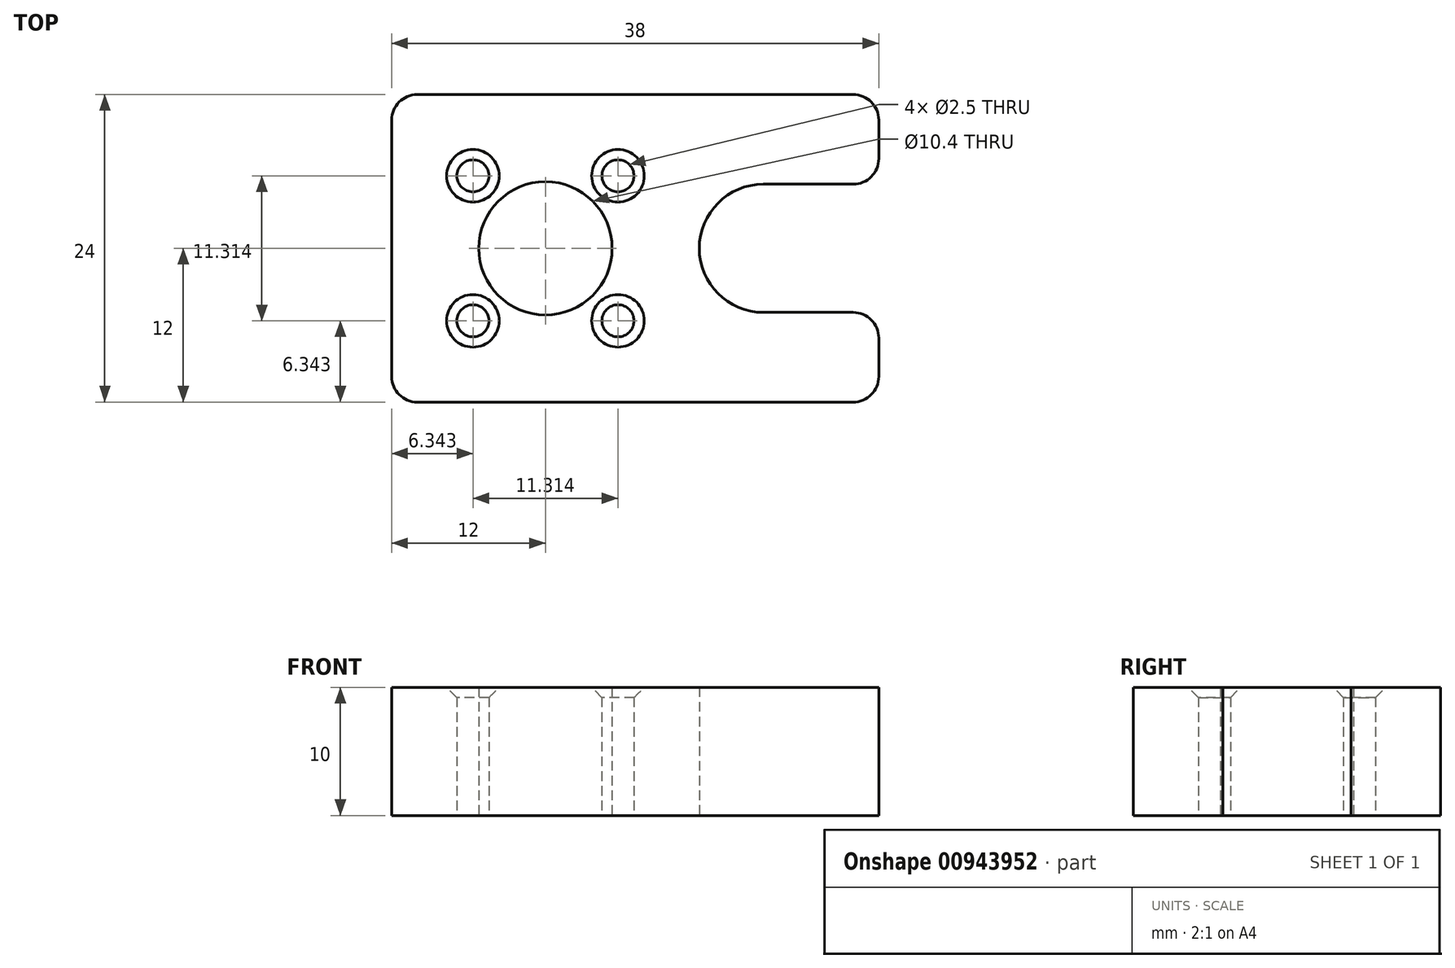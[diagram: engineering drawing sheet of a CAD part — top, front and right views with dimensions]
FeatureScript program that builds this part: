
annotation { "Feature Type Name" : "Feature", "Feature Type Description" : "" }
export const myFeature = defineFeature(function(context is Context, id is Id, definition is map)
    precondition{}
    {
        {
            var Q0;
            Q0=qCreatedBy(makeId("Top.planeOp"),FACE);
            var sketch = newSketch(context, id + "F0", { "sketchPlane" : qUnion([Q0])});
            skLineSegment(sketch, "E0.bottom", {"start": v(19, 12) * mm, "end": v(-19, 12) * mm});
            skLineSegment(sketch, "E0.top", {"start": v(19, -12) * mm, "end": v(-19, -12) * mm});
            skLineSegment(sketch, "E0.left", {"start": v(19, 12) * mm, "end": v(19, 5) * mm});
            skLineSegment(sketch, "E0.right", {"start": v(-19, 12) * mm, "end": v(-19, -12) * mm});
            skPoint(sketch, "E0.middle", {"position": v(0, 0) * mm});
            skCircle(sketch, "E1", {"center": v(-7, 0) * mm, "radius": 5.2 * mm});
            skCircle(sketch, "E2", {"center": v(10, 0) * mm, "radius": 5 * mm, "construction": true});
            skLineSegment(sketch, "E3", {"start": v(10, 5) * mm, "end": v(19, 5) * mm});
            skLineSegment(sketch, "E4", {"start": v(10, -5) * mm, "end": v(19, -5) * mm});
            skArc(sketch, "E5", {"start": v(10, 5) * mm, "mid": v(5, 0) * mm, "end": v(10, -5) * mm});
            skLineSegment(sketch, "E6.trimOffspring", {"start": v(19, -5) * mm, "end": v(19, -12) * mm});
            skCircle(sketch, "E7", {"center": v(-7, 0) * mm, "radius": 8 * mm, "construction": true});
            skLineSegment(sketch, "E8.bottom", {"start": v(-12.66, 5.66) * mm, "end": v(-1.34, 5.66) * mm, "construction": true});
            skLineSegment(sketch, "E8.top", {"start": v(-12.66, -5.66) * mm, "end": v(-1.34, -5.66) * mm, "construction": true});
            skLineSegment(sketch, "E8.left", {"start": v(-12.66, 5.66) * mm, "end": v(-12.66, -5.66) * mm, "construction": true});
            skLineSegment(sketch, "E8.right", {"start": v(-1.34, 5.66) * mm, "end": v(-1.34, -5.66) * mm, "construction": true});
            skCircle(sketch, "E9", {"center": v(-12.66, 5.66) * mm, "radius": 1.25 * mm});
            skCircle(sketch, "E10", {"center": v(-1.34, 5.66) * mm, "radius": 1.25 * mm});
            skCircle(sketch, "E11", {"center": v(-12.66, -5.66) * mm, "radius": 1.25 * mm});
            skCircle(sketch, "E12", {"center": v(-1.34, -5.66) * mm, "radius": 1.25 * mm});
            skCircle(sketch, "E13", {"center": v(-7, 0) * mm, "radius": 11 * mm, "construction": true});
            skSolve(sketch);
        }
        {
            var Q0;
            Q0 = qSketchRegion(id + "F0", true);
            extrude(context, id + "F1", {"entities" : qUnion([Q0]), "depth" : 10 * mm, "offsetDistance" : 25 * mm});
        }
        {
            var Q0;
            Q0=makeQuery(id+"F1.opExtrude","SWEPT_EDGE",EDGE,{"disambiguationData":[OSD([sQuery(id+"F0.wireOp",EDGE,"E0.top"),sQuery(id+"F0.wireOp",EDGE,"E0.right")])]});
            var Q1;
            Q1=makeQuery(id+"F1.opExtrude","SWEPT_EDGE",EDGE,{"disambiguationData":[OSD([sQuery(id+"F0.wireOp",EDGE,"E0.bottom"),sQuery(id+"F0.wireOp",EDGE,"E0.right")])]});
            var Q2;
            Q2=makeQuery(id+"F1.opExtrude","SWEPT_EDGE",EDGE,{"disambiguationData":[OSD([sQuery(id+"F0.wireOp",EDGE,"E0.top"),sQuery(id+"F0.wireOp",EDGE,"E6.trimOffspring")])]});
            var Q3;
            Q3=makeQuery(id+"F1.opExtrude","SWEPT_EDGE",EDGE,{"disambiguationData":[OSD([sQuery(id+"F0.wireOp",EDGE,"E4"),sQuery(id+"F0.wireOp",EDGE,"E6.trimOffspring")])]});
            var Q4;
            Q4=makeQuery(id+"F1.opExtrude","SWEPT_EDGE",EDGE,{"disambiguationData":[OSD([sQuery(id+"F0.wireOp",EDGE,"E0.left"),sQuery(id+"F0.wireOp",EDGE,"E3")])]});
            var Q5;
            Q5=makeQuery(id+"F1.opExtrude","SWEPT_EDGE",EDGE,{"disambiguationData":[OSD([sQuery(id+"F0.wireOp",EDGE,"E0.bottom"),sQuery(id+"F0.wireOp",EDGE,"E0.left")])]});
            fillet(context, id + "F2", {"entities" : qUnion([Q0, Q1, Q2, Q3, Q4, Q5]), "radius" : 2 * mm, "tangentPropagation" : true, "allowEdgeOverflow" : false});
        }
        {
            var Q0;
            Q0=makeQuery(id+"F1.opExtrude","CAP_EDGE",EDGE,{"disambiguationData":[OSD([sQuery(id+"F0.wireOp",EDGE,"E9")])],"isStart":false});
            var Q1;
            Q1=makeQuery(id+"F1.opExtrude","CAP_EDGE",EDGE,{"disambiguationData":[OSD([sQuery(id+"F0.wireOp",EDGE,"E10")])],"isStart":false});
            var Q2;
            Q2=makeQuery(id+"F1.opExtrude","CAP_EDGE",EDGE,{"disambiguationData":[OSD([sQuery(id+"F0.wireOp",EDGE,"E12")])],"isStart":false});
            var Q3;
            Q3=makeQuery(id+"F1.opExtrude","CAP_EDGE",EDGE,{"disambiguationData":[OSD([sQuery(id+"F0.wireOp",EDGE,"E11")])],"isStart":false});
            chamfer(context, id + "F3", {"entities" : qUnion([Q0, Q1, Q2, Q3]), "width" : 0.8 * mm, "tangentPropagation" : true});
        }
    });
